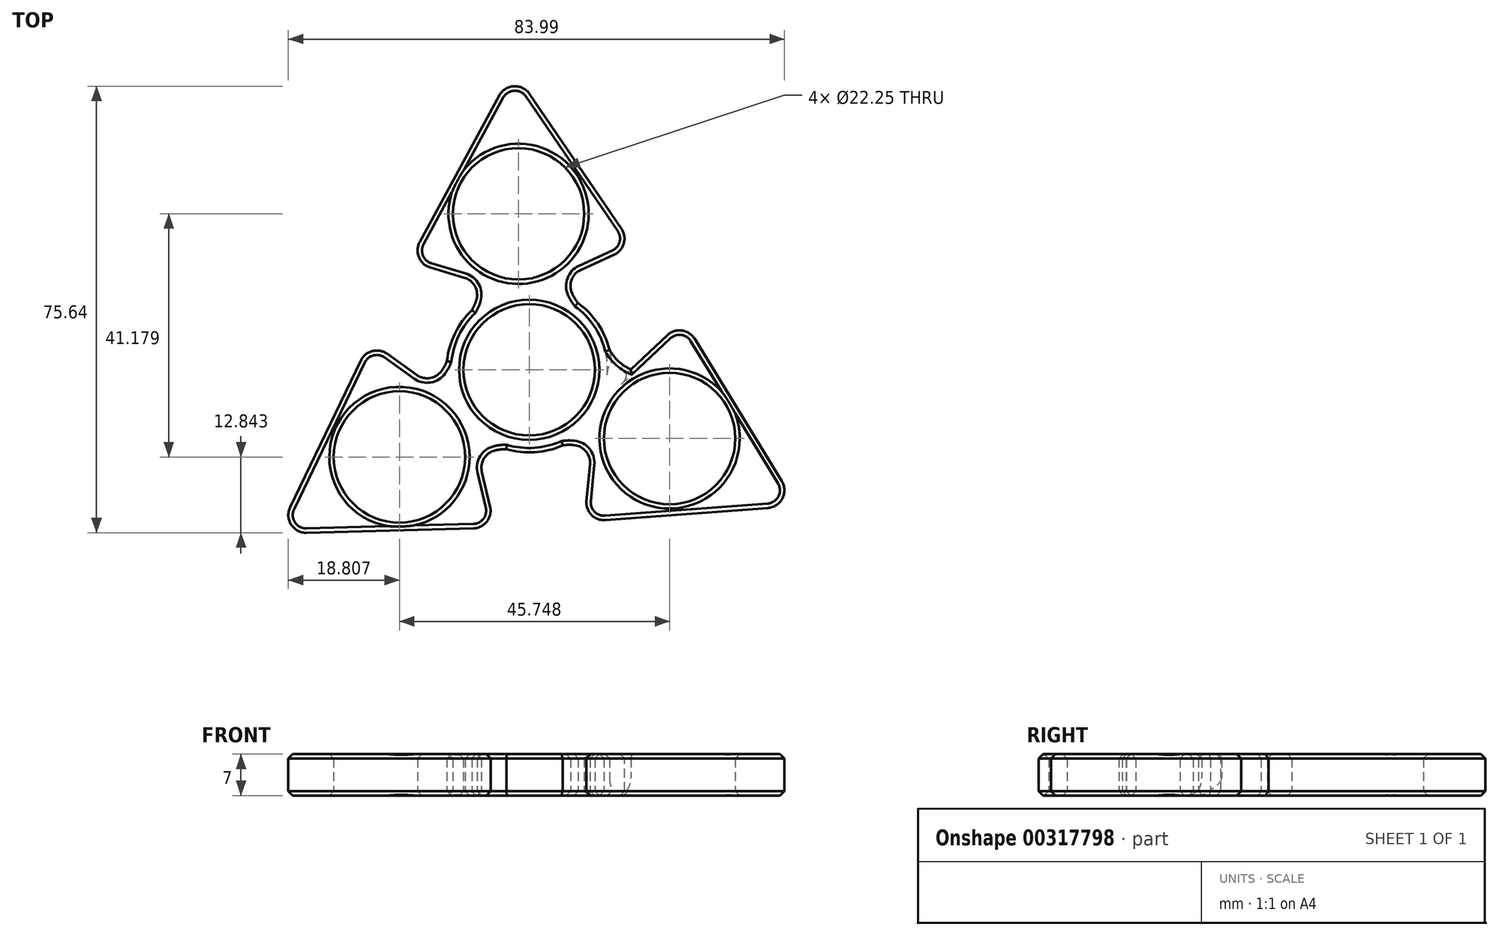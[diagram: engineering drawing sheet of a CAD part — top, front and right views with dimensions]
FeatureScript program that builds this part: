
annotation { "Feature Type Name" : "Feature", "Feature Type Description" : "" }
export const myFeature = defineFeature(function(context is Context, id is Id, definition is map)
    precondition{}
    {
        {
            var Q0;
            Q0=qCreatedBy(makeId("Top.planeOp"),FACE);
            var sketch = newSketch(context, id + "F0", { "sketchPlane" : qUnion([Q0])});
            skCircle(sketch, "E0", {"center": v(0, 0) * mm, "radius": 11.12 * mm});
            skCircle(sketch, "E1", {"center": v(0, 0) * mm, "radius": 14 * mm});
            skPoint(sketch, "E2", {"position": v(-9.7, 10.09) * mm});
            skPoint(sketch, "E3", {"position": v(8.25, 11.31) * mm});
            skLineSegment(sketch, "E4", {"start": v(-9.7, 10.09) * mm, "end": v(8.25, 11.31) * mm, "construction": true});
            skLineSegment(sketch, "E5", {"start": v(8.25, 11.31) * mm, "end": v(7.64, 20.3) * mm, "construction": true});
            skLineSegment(sketch, "E6", {"start": v(-9.7, 10.09) * mm, "end": v(-10.32, 19.07) * mm, "construction": true});
            skLineSegment(sketch, "E7", {"start": v(-10.32, 19.07) * mm, "end": v(7.64, 20.3) * mm});
            skArc(sketch, "E8", {"start": v(-9.7, 10.09) * mm, "mid": v(-8.63, 14.67) * mm, "end": v(-10.32, 19.07) * mm});
            skArc(sketch, "E9", {"start": v(7.64, 20.3) * mm, "mid": v(6.56, 15.7) * mm, "end": v(8.25, 11.31) * mm});
            skLineSegment(sketch, "E10", {"start": v(-10.32, 19.07) * mm, "end": v(-20.3, 18.38) * mm});
            skLineSegment(sketch, "E11", {"start": v(7.64, 20.3) * mm, "end": v(17.61, 20.97) * mm});
            skPoint(sketch, "E12", {"position": v(-1.34, 19.68) * mm});
            skPoint(sketch, "E13", {"position": v(-1.8, 26.41) * mm});
            skCircle(sketch, "E14", {"center": v(-1.8, 26.41) * mm, "radius": 11.12 * mm});
            skLineSegment(sketch, "E15", {"start": v(-1.34, 19.68) * mm, "end": v(-1.8, 26.41) * mm, "construction": true});
            skLineSegment(sketch, "E16", {"start": v(-1.8, 26.41) * mm, "end": v(-2.71, 39.76) * mm, "construction": true});
            skPoint(sketch, "E17", {"position": v(-8.65, 14.89) * mm});
            skPoint(sketch, "E18", {"position": v(6.55, 15.92) * mm});
            skLineSegment(sketch, "E19", {"start": v(-8.65, 14.89) * mm, "end": v(-20.3, 18.38) * mm});
            skLineSegment(sketch, "E20", {"start": v(6.55, 15.92) * mm, "end": v(17.61, 20.97) * mm});
            skLineSegment(sketch, "E21", {"start": v(-20.3, 18.38) * mm, "end": v(-2.71, 50.78) * mm});
            skLineSegment(sketch, "E22", {"start": v(-2.71, 50.78) * mm, "end": v(17.61, 20.97) * mm});
            skPoint(sketch, "E23.center", {"position": v(0.2, -3) * mm});
            skCircle(sketch, "E24", {"center": v(0, 0) * mm, "radius": 51.15 * mm, "construction": true});
            skArc(sketch, "E25.1.0", {"start": v(-3.88, -13.45) * mm, "mid": v(-8.39, -14.81) * mm, "end": v(-11.35, -18.47) * mm});
            skArc(sketch, "E25.1.1", {"start": v(-21.4, -3.53) * mm, "mid": v(-16.88, -2.17) * mm, "end": v(-13.92, 1.49) * mm});
            skCircle(sketch, "E25.1.2", {"center": v(-21.97, -14.77) * mm, "radius": 11.12 * mm});
            skLineSegment(sketch, "E25.1.3", {"start": v(-8.57, -14.94) * mm, "end": v(-5.77, -26.77) * mm});
            skLineSegment(sketch, "E25.1.4", {"start": v(-11.35, -18.47) * mm, "end": v(-5.77, -26.77) * mm});
            skLineSegment(sketch, "E25.1.5", {"start": v(-5.77, -26.77) * mm, "end": v(-42.62, -27.74) * mm});
            skLineSegment(sketch, "E25.1.6", {"start": v(-42.62, -27.74) * mm, "end": v(-26.97, 4.77) * mm});
            skLineSegment(sketch, "E25.1.7", {"start": v(-21.4, -3.53) * mm, "end": v(-26.97, 4.77) * mm});
            skLineSegment(sketch, "E25.1.8", {"start": v(-11.35, -18.47) * mm, "end": v(-21.4, -3.53) * mm});
            skLineSegment(sketch, "E25.1.9", {"start": v(-17.07, -2.3) * mm, "end": v(-26.97, 4.77) * mm});
            skArc(sketch, "E25.2.0", {"start": v(13.59, 3.37) * mm, "mid": v(17.02, 0.14) * mm, "end": v(21.67, -0.6) * mm});
            skArc(sketch, "E25.2.1", {"start": v(13.75, -16.76) * mm, "mid": v(10.32, -13.53) * mm, "end": v(5.67, -12.8) * mm});
            skCircle(sketch, "E25.2.2", {"center": v(23.77, -11.65) * mm, "radius": 11.12 * mm});
            skLineSegment(sketch, "E25.2.3", {"start": v(17.22, 0.05) * mm, "end": v(26.07, 8.39) * mm});
            skLineSegment(sketch, "E25.2.4", {"start": v(21.67, -0.6) * mm, "end": v(26.07, 8.39) * mm});
            skLineSegment(sketch, "E25.2.5", {"start": v(26.07, 8.39) * mm, "end": v(45.33, -23.04) * mm});
            skLineSegment(sketch, "E25.2.6", {"start": v(45.33, -23.04) * mm, "end": v(9.36, -25.74) * mm});
            skLineSegment(sketch, "E25.2.7", {"start": v(13.75, -16.76) * mm, "end": v(9.36, -25.74) * mm});
            skLineSegment(sketch, "E25.2.8", {"start": v(21.67, -0.6) * mm, "end": v(13.75, -16.76) * mm});
            skLineSegment(sketch, "E25.2.9", {"start": v(10.52, -13.63) * mm, "end": v(9.36, -25.74) * mm});
            skSolve(sketch);
        }
        {
            var Q0;
            Q0 = qSketchRegion(id + "F0", true);
            extrude(context, id + "F1", {"entities" : qUnion([Q0]), "depth" : 7 * mm});
        }
        {
            var Q0;
            Q0=makeQuery(id+"F1.opExtrude","SWEPT_EDGE",EDGE,{"disambiguationData":[OSD([sQuery(id+"F0.wireOp",EDGE,"E25.2.5"),sQuery(id+"F0.wireOp",EDGE,"E25.2.6")])]});
            var Q1;
            Q1=makeQuery(id+"F1.opExtrude","SWEPT_EDGE",EDGE,{"disambiguationData":[OSD([sQuery(id+"F0.wireOp",EDGE,"E25.1.5"),sQuery(id+"F0.wireOp",EDGE,"E25.1.6")])]});
            var Q2;
            Q2=makeQuery(id+"F1.opExtrude","SWEPT_EDGE",EDGE,{"disambiguationData":[OSD([sQuery(id+"F0.wireOp",EDGE,"E21"),sQuery(id+"F0.wireOp",EDGE,"E22")])]});
            var Q3;
            Q3=makeQuery(id+"F1.opExtrude","SWEPT_EDGE",EDGE,{"disambiguationData":[OSD([sQuery(id+"F0.wireOp",EDGE,"E11"),sQuery(id+"F0.wireOp",EDGE,"E20"),sQuery(id+"F0.wireOp",EDGE,"E22")])]});
            var Q4;
            Q4=makeQuery(id+"F1.opExtrude","SWEPT_EDGE",EDGE,{"disambiguationData":[OSD([sQuery(id+"F0.wireOp",EDGE,"E10"),sQuery(id+"F0.wireOp",EDGE,"E19"),sQuery(id+"F0.wireOp",EDGE,"E21")])]});
            var Q5;
            Q5=makeQuery(id+"F1.opExtrude","SWEPT_EDGE",EDGE,{"disambiguationData":[OSD([sQuery(id+"F0.wireOp",EDGE,"E25.1.6"),sQuery(id+"F0.wireOp",EDGE,"E25.1.7"),sQuery(id+"F0.wireOp",EDGE,"E25.1.9")])]});
            var Q6;
            Q6=makeQuery(id+"F1.opExtrude","SWEPT_EDGE",EDGE,{"disambiguationData":[OSD([sQuery(id+"F0.wireOp",EDGE,"E25.1.3"),sQuery(id+"F0.wireOp",EDGE,"E25.1.4"),sQuery(id+"F0.wireOp",EDGE,"E25.1.5")])]});
            var Q7;
            Q7=makeQuery(id+"F1.opExtrude","SWEPT_EDGE",EDGE,{"disambiguationData":[OSD([sQuery(id+"F0.wireOp",EDGE,"E25.2.6"),sQuery(id+"F0.wireOp",EDGE,"E25.2.7"),sQuery(id+"F0.wireOp",EDGE,"E25.2.9")])]});
            var Q8;
            Q8=makeQuery(id+"F1.opExtrude","SWEPT_EDGE",EDGE,{"disambiguationData":[OSD([sQuery(id+"F0.wireOp",EDGE,"E25.2.3"),sQuery(id+"F0.wireOp",EDGE,"E25.2.4"),sQuery(id+"F0.wireOp",EDGE,"E25.2.5")])]});
            var Q9;
            Q9=makeQuery(id+"F1.opExtrude","SWEPT_EDGE",EDGE,{"disambiguationData":[OSD([sQuery(id+"F0.wireOp",EDGE,"E9"),sQuery(id+"F0.wireOp",EDGE,"E20")])]});
            var Q10;
            Q10=makeQuery(id+"F1.opExtrude","CAP_EDGE",EDGE,{"disambiguationData":[OSD([sQuery(id+"F0.wireOp",EDGE,"E25.2.0")])],"isStart":true});
            var Q11;
            Q11=makeQuery(id+"F1.opExtrude","SWEPT_EDGE",EDGE,{"disambiguationData":[OSD([sQuery(id+"F0.wireOp",EDGE,"E25.2.1"),sQuery(id+"F0.wireOp",EDGE,"E25.2.9")])]});
            var Q12;
            Q12=makeQuery(id+"F1.opExtrude","SWEPT_EDGE",EDGE,{"disambiguationData":[OSD([sQuery(id+"F0.wireOp",EDGE,"E25.1.0"),sQuery(id+"F0.wireOp",EDGE,"E25.1.3")])]});
            var Q13;
            Q13=makeQuery(id+"F1.opExtrude","SWEPT_EDGE",EDGE,{"disambiguationData":[OSD([sQuery(id+"F0.wireOp",EDGE,"E25.1.1"),sQuery(id+"F0.wireOp",EDGE,"E25.1.9")])]});
            var Q14;
            Q14=makeQuery(id+"F1.opExtrude","SWEPT_EDGE",EDGE,{"disambiguationData":[OSD([sQuery(id+"F0.wireOp",EDGE,"E8"),sQuery(id+"F0.wireOp",EDGE,"E19")])]});
            fillet(context, id + "F2", {"entities" : qUnion([Q0, Q1, Q2, Q3, Q4, Q5, Q6, Q7, Q8, Q9, Q10, Q11, Q12, Q13, Q14]), "radius" : 3 * mm, "tangentPropagation" : true, "allowEdgeOverflow" : false});
        }
        {
            var Q0;
            Q0=makeQuery(id+"F1.opExtrude","CAP_FACE",FACE,{"disambiguationData":[OSD([sQuery(id+"F0.wireOp",EDGE,"E0"),sQuery(id+"F0.wireOp",EDGE,"E1"),sQuery(id+"F0.wireOp",EDGE,"E8"),sQuery(id+"F0.wireOp",EDGE,"E9"),sQuery(id+"F0.wireOp",EDGE,"E14"),sQuery(id+"F0.wireOp",EDGE,"E19"),sQuery(id+"F0.wireOp",EDGE,"E20"),sQuery(id+"F0.wireOp",EDGE,"E21"),sQuery(id+"F0.wireOp",EDGE,"E22"),sQuery(id+"F0.wireOp",EDGE,"E25.1.0"),sQuery(id+"F0.wireOp",EDGE,"E25.1.1"),sQuery(id+"F0.wireOp",EDGE,"E25.1.2"),sQuery(id+"F0.wireOp",EDGE,"E25.1.3"),sQuery(id+"F0.wireOp",EDGE,"E25.1.5"),sQuery(id+"F0.wireOp",EDGE,"E25.1.6"),sQuery(id+"F0.wireOp",EDGE,"E25.1.9"),sQuery(id+"F0.wireOp",EDGE,"E25.2.0"),sQuery(id+"F0.wireOp",EDGE,"E25.2.1"),sQuery(id+"F0.wireOp",EDGE,"E25.2.2"),sQuery(id+"F0.wireOp",EDGE,"E25.2.3"),sQuery(id+"F0.wireOp",EDGE,"E25.2.5"),sQuery(id+"F0.wireOp",EDGE,"E25.2.6"),sQuery(id+"F0.wireOp",EDGE,"E25.2.9")])],"isStart":true});
            var Q1;
            Q1=makeQuery(id+"F1.opExtrude","CAP_FACE",FACE,{"disambiguationData":[OSD([sQuery(id+"F0.wireOp",EDGE,"E0"),sQuery(id+"F0.wireOp",EDGE,"E1"),sQuery(id+"F0.wireOp",EDGE,"E8"),sQuery(id+"F0.wireOp",EDGE,"E9"),sQuery(id+"F0.wireOp",EDGE,"E14"),sQuery(id+"F0.wireOp",EDGE,"E19"),sQuery(id+"F0.wireOp",EDGE,"E20"),sQuery(id+"F0.wireOp",EDGE,"E21"),sQuery(id+"F0.wireOp",EDGE,"E22"),sQuery(id+"F0.wireOp",EDGE,"E25.1.0"),sQuery(id+"F0.wireOp",EDGE,"E25.1.1"),sQuery(id+"F0.wireOp",EDGE,"E25.1.2"),sQuery(id+"F0.wireOp",EDGE,"E25.1.3"),sQuery(id+"F0.wireOp",EDGE,"E25.1.5"),sQuery(id+"F0.wireOp",EDGE,"E25.1.6"),sQuery(id+"F0.wireOp",EDGE,"E25.1.9"),sQuery(id+"F0.wireOp",EDGE,"E25.2.0"),sQuery(id+"F0.wireOp",EDGE,"E25.2.1"),sQuery(id+"F0.wireOp",EDGE,"E25.2.2"),sQuery(id+"F0.wireOp",EDGE,"E25.2.3"),sQuery(id+"F0.wireOp",EDGE,"E25.2.5"),sQuery(id+"F0.wireOp",EDGE,"E25.2.6"),sQuery(id+"F0.wireOp",EDGE,"E25.2.9")])],"isStart":false});
            chamfer(context, id + "F3", {"entities" : qUnion([Q0, Q1]), "width" : .75 * mm, "tangentPropagation" : true});
        }
    });
